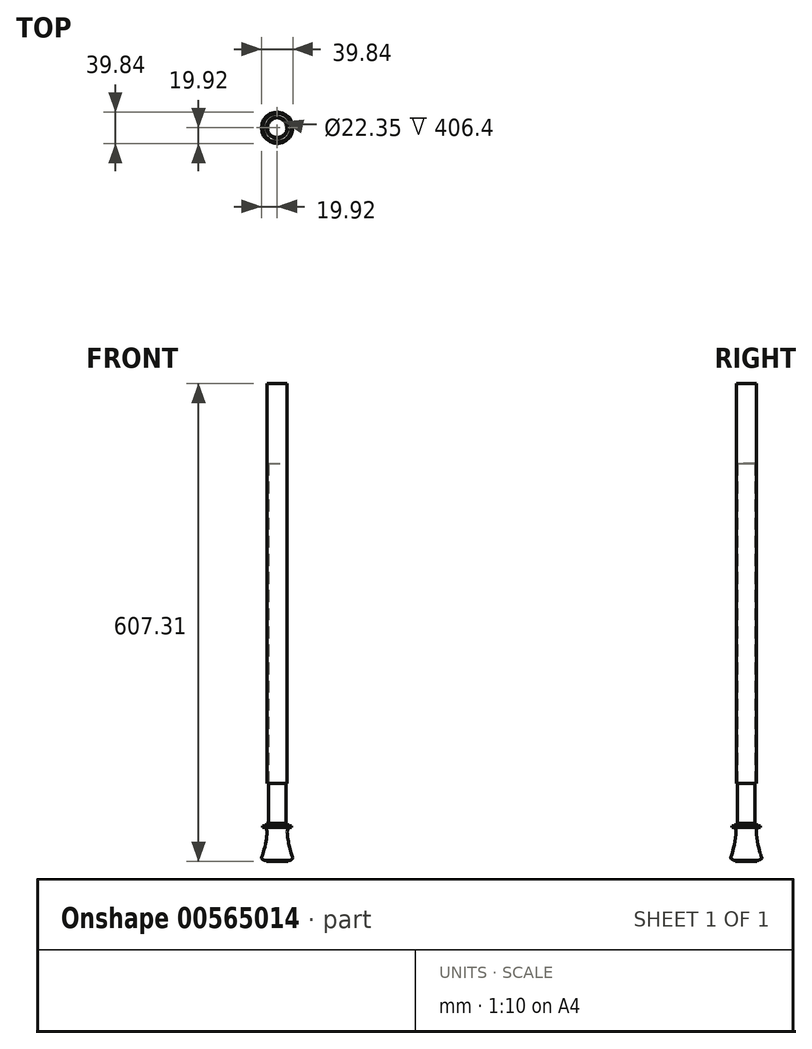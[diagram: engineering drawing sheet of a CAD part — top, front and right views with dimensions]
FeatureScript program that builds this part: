
annotation { "Feature Type Name" : "Feature", "Feature Type Description" : "" }
export const myFeature = defineFeature(function(context is Context, id is Id, definition is map)
    precondition{}
    {
        {
            var Q0;
            Q0=qCreatedBy(makeId("Front.planeOp"),FACE);
            var sketch = newSketch(context, id + "F0", { "sketchPlane" : qUnion([Q0])});
            skLineSegment(sketch, "E0", {"start": v(0, 0) * mm, "end": v(-12.7, 0) * mm});
            skLineSegment(sketch, "E1", {"start": v(-12.7, 0) * mm, "end": v(-12.7, -476.25) * mm});
            skLineSegment(sketch, "E2", {"start": v(-12.7, -476.25) * mm, "end": v(0, -476.25) * mm});
            skLineSegment(sketch, "E3", {"start": v(0, -476.25) * mm, "end": v(0, 0) * mm});
            skLineSegment(sketch, "E4", {"start": v(0, 0) * mm, "end": v(12.7, 0) * mm, "construction": true});
            skLineSegment(sketch, "E5", {"start": v(12.7, 0) * mm, "end": v(12.7, -476.25) * mm, "construction": true});
            skLineSegment(sketch, "E6", {"start": v(0, -476.25) * mm, "end": v(-11.18, -476.25) * mm, "construction": true});
            skLineSegment(sketch, "E7", {"start": v(-11.18, -476.25) * mm, "end": v(-11.18, -527.05) * mm});
            skLineSegment(sketch, "E8", {"start": v(-11.18, -527.05) * mm, "end": v(0, -527.05) * mm});
            skLineSegment(sketch, "E9", {"start": v(0, -527.05) * mm, "end": v(0, -476.25) * mm});
            skLineSegment(sketch, "E10", {"start": v(0, -527.05) * mm, "end": v(11.18, -527.05) * mm, "construction": true});
            skLineSegment(sketch, "E11", {"start": v(0, -476.25) * mm, "end": v(12.7, -476.25) * mm, "construction": true});
            skLineSegment(sketch, "E12", {"start": v(11.18, -527.05) * mm, "end": v(11.18, -476.25) * mm, "construction": true});
            skLineSegment(sketch, "E13", {"start": v(0, -527.05) * mm, "end": v(0, -575.56) * mm});
            skLineSegment(sketch, "E14", {"start": v(0, -527.05) * mm, "end": v(-13.2, -527.05) * mm});
            skLineSegment(sketch, "E15", {"start": v(-13.2, -527.05) * mm, "end": v(-13.2, -530.35) * mm});
            skLineSegment(sketch, "E16", {"start": v(0, -530.35) * mm, "end": v(-18.29, -530.35) * mm, "construction": true});
            skLineSegment(sketch, "E17", {"start": v(-18.29, -530.35) * mm, "end": v(-18.29, -532.13) * mm});
            skLineSegment(sketch, "E18", {"start": v(-18.29, -532.13) * mm, "end": v(-14.73, -532.13) * mm, "construction": true});
            skLineSegment(sketch, "E19", {"start": v(0, -575.56) * mm, "end": v(-13.59, -575.56) * mm});
            skLineSegment(sketch, "E20", {"start": v(-13.59, -575.56) * mm, "end": v(-13.59, -574.04) * mm});
            skLineSegment(sketch, "E21", {"start": v(-13.59, -574.04) * mm, "end": v(-16.13, -574.04) * mm});
            skLineSegment(sketch, "E22", {"start": v(-13.59, -574.04) * mm, "end": v(-13.59, -568.45) * mm, "construction": true});
            skLineSegment(sketch, "E23", {"start": v(-13.59, -568.45) * mm, "end": v(0, -568.45) * mm, "construction": true});
            skLineSegment(sketch, "E24", {"start": v(0, -568.45) * mm, "end": v(-19.05, -568.45) * mm, "construction": true});
            skLineSegment(sketch, "E25", {"start": v(-19.05, -568.45) * mm, "end": v(-19.05, -571.25) * mm, "construction": true});
            skLineSegment(sketch, "E26", {"start": v(-19.05, -571.25) * mm, "end": v(-19.81, -571.25) * mm, "construction": true});
            skLineSegment(sketch, "E27", {"start": v(0, -532.13) * mm, "end": v(-14.73, -532.13) * mm, "construction": true});
            skLineSegment(sketch, "E28", {"start": v(0, -532.13) * mm, "end": v(0, -538.48) * mm, "construction": true});
            skLineSegment(sketch, "E29", {"start": v(0, -538.48) * mm, "end": v(-12.83, -538.48) * mm, "construction": true});
            skFitSpline(sketch, "E30", {"points": [v(-14.73, -532.13) * mm, v(-12.83, -538.48) * mm, v(-19.05, -568.45) * mm, v(-19.81, -571.25) * mm, v(-16.13, -574.04) * mm], "startDerivative": vector(13.1, -19.84) * mm, "endDerivative": vector(27.3, -16.59) * mm});
            skLineSegment(sketch, "E31", {"start": v(-18.29, -532.13) * mm, "end": v(-14.73, -532.13) * mm});
            skLineSegment(sketch, "E32", {"start": v(0, -527.05) * mm, "end": v(0, 0) * mm});
            skLineSegment(sketch, "E33", {"start": v(0, -263.53) * mm, "end": v(25.4, -263.53) * mm, "construction": true});
            skLineSegment(sketch, "E34.MirrorCS", {"start": v(0, 0) * mm, "end": v(0, 48.51) * mm});
            skLineSegment(sketch, "E35", {"start": v(-18.29, -530.35) * mm, "end": v(-13.2, -530.35) * mm});
            skLineSegment(sketch, "E36", {"start": v(-11.18, -476.25) * mm, "end": v(-11.18, -69.85) * mm});
            skLineSegment(sketch, "E37", {"start": v(-11.18, -69.85) * mm, "end": v(0, -69.85) * mm});
            skLineSegment(sketch, "E38", {"start": v(0, 0) * mm, "end": v(0, 31.75) * mm});
            skLineSegment(sketch, "E39", {"start": v(0, 31.75) * mm, "end": v(-12.7, 31.75) * mm});
            skLineSegment(sketch, "E40", {"start": v(-12.7, 0) * mm, "end": v(-12.7, 31.75) * mm});
            skPoint(sketch, "E41.MirrorCS.end.orphan", {"position": v(-13.2, 3.3) * mm});
            skPoint(sketch, "E41.MirrorCS.start.orphan", {"position": v(-13.2, 0) * mm});
            skSolve(sketch);
        }
        {
            var Q0;
            Q0=makeQuery(id+"F0.imprint","IMPRINT",FACE,{"disambiguationData":[TD([[makeQuery(id+"F0.imprint","IMPRINT",EDGE,{"derivedFrom":sQuery(id+"F0.wireOp",EDGE,"E0")}),-1.0]])]});
            var Q1;
            {var subQ4=sQuery(id+"F0.wireOp",EDGE,"E1");Q1=makeQuery(id+"F0.imprint","IMPRINT",FACE,{"disambiguationData":[TD([[makeQuery(id+"F0.imprint","IMPRINT",EDGE,{"derivedFrom":subQ4}),1.0]])]});}
            var Q2;
            Q2=sQuery(id+"F0.wireOp",EDGE,"E34.MirrorCS");
            revolve(context, id + "F1", {"entities" : qUnion([Q0, Q1]), "axis" : qUnion([Q2]), "revolveType" : RevolveType.FULL});
        }
        {
            var Q0;
            {var subQ0=sQuery(id+"F0.wireOp",EDGE,"E13");Q0=makeQuery(id+"F0.imprint","IMPRINT",FACE,{"disambiguationData":[TD([[makeQuery(id+"F0.imprint","IMPRINT",EDGE,{"derivedFrom":subQ0}),-1.0]])]});}
            var Q1;
            {var subQ3=sQuery(id+"F0.wireOp",EDGE,"E7");Q1=makeQuery(id+"F0.imprint","IMPRINT",FACE,{"disambiguationData":[TD([[makeQuery(id+"F0.imprint","IMPRINT",EDGE,{"derivedFrom":subQ3}),1.0]])]});}
            var Q2;
            {var subQ3=sQuery(id+"F0.wireOp",EDGE,"E36");Q2=makeQuery(id+"F0.imprint","IMPRINT",FACE,{"disambiguationData":[TD([[makeQuery(id+"F0.imprint","IMPRINT",EDGE,{"derivedFrom":subQ3}),-1.0]])]});}
            var Q3;
            Q3=sQuery(id+"F0.wireOp",EDGE,"E32");
            revolve(context, id + "F2", {"entities" : qUnion([Q0, Q1, Q2]), "axis" : qUnion([Q3]), "revolveType" : RevolveType.FULL});
        }
    });
